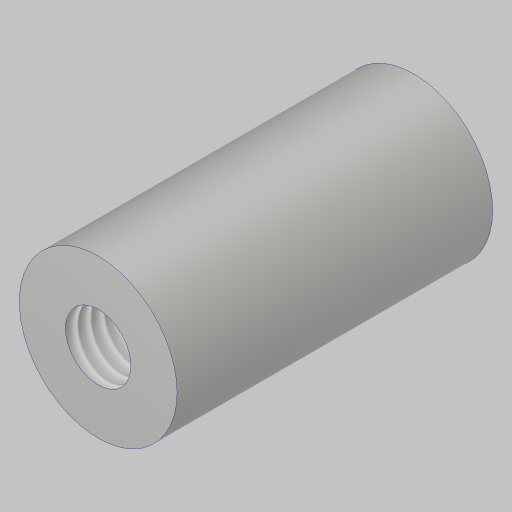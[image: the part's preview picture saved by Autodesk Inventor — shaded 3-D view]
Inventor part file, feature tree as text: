
AUTODESK INVENTOR PART (.ipt)
format: ipt  version: 2023.5 (Build 275446000, 446)  size: 121,856 bytes
history: native  units: in
note: dims shown in document units (in); Inventor stores cm internally (conversion verified against a paired STEP export)
features: extrude x1, hole x1
ambient origin geometry x8: Origin, YZ Plane, XZ Plane, XY Plane, X Axis, Y Axis, Z Axis, Center Point
bodies: Solid1 (feature_tree)
feature tree (2):
  extrude  "Extrusion1"  Depth=0.75in
  hole  "Hole1"  [1 undecoded]
note: 1 required parameter value undecoded (feature->parameter linkage not recoverable at this tier; creation-order binding heuristic only, values carry confidence <= 0.55)
